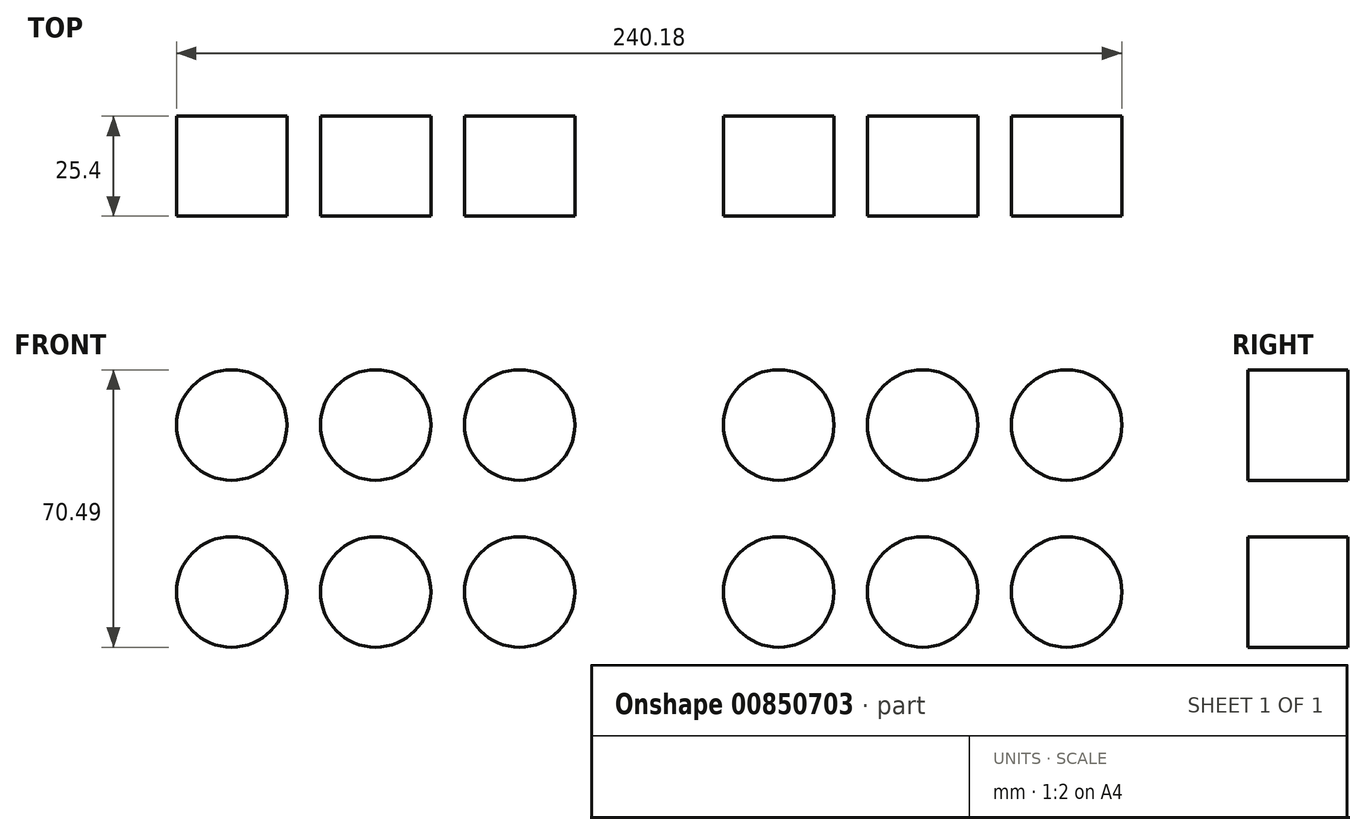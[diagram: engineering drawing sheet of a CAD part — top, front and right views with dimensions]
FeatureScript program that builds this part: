
annotation { "Feature Type Name" : "Feature", "Feature Type Description" : "" }
export const myFeature = defineFeature(function(context is Context, id is Id, definition is map)
    precondition{}
    {
        {
            var Q0;
            Q0=qCreatedBy(makeId("Front.planeOp"),FACE);
            var sketch = newSketch(context, id + "F0", { "sketchPlane" : qUnion([Q0])});
            skCircle(sketch, "E0", {"center": v(-106.05, -5.51) * mm, "radius": 14.04 * mm});
            skCircle(sketch, "E1.0.1.0", {"center": v(-106.05, 36.9) * mm, "radius": 14.04 * mm});
            skCircle(sketch, "E1.1.0.0", {"center": v(-69.48, -5.51) * mm, "radius": 14.04 * mm});
            skCircle(sketch, "E1.1.1.0", {"center": v(-69.48, 36.9) * mm, "radius": 14.04 * mm});
            skCircle(sketch, "E1.2.0.0", {"center": v(-32.9, -5.51) * mm, "radius": 14.04 * mm});
            skCircle(sketch, "E1.2.1.0", {"center": v(-32.9, 36.9) * mm, "radius": 14.04 * mm});
            skLineSegment(sketch, "E1.direction1", {"start": v(-106.05, -5.51) * mm, "end": v(-69.48, -5.51) * mm, "construction": true});
            skLineSegment(sketch, "E1.direction2", {"start": v(-106.05, -5.51) * mm, "end": v(-106.05, 36.9) * mm, "construction": true});
            skCircle(sketch, "E2.MirrorC", {"center": v(69.48, 36.9) * mm, "radius": 14.04 * mm});
            skCircle(sketch, "E3.MirrorC", {"center": v(69.48, -5.51) * mm, "radius": 14.04 * mm});
            skCircle(sketch, "E4.MirrorC", {"center": v(106.05, 36.9) * mm, "radius": 14.04 * mm});
            skCircle(sketch, "E5.MirrorC", {"center": v(106.05, -5.51) * mm, "radius": 14.04 * mm});
            skLineSegment(sketch, "E6.MirrorCS", {"start": v(106.05, -5.51) * mm, "end": v(106.05, 36.9) * mm, "construction": true});
            skCircle(sketch, "E7.MirrorC", {"center": v(32.9, 36.9) * mm, "radius": 14.04 * mm});
            skLineSegment(sketch, "E8.MirrorCS", {"start": v(106.05, -5.51) * mm, "end": v(69.48, -5.51) * mm, "construction": true});
            skCircle(sketch, "E9.MirrorC", {"center": v(32.9, -5.51) * mm, "radius": 14.04 * mm});
            skSolve(sketch);
        }
        {
            var Q0;
            Q0 = qSketchRegion(id + "F0", true);
            extrude(context, id + "F1", {"entities" : qUnion([Q0]), "depth" : 25.4 * mm, "offsetDistance" : 25.4 * mm});
        }
    });
